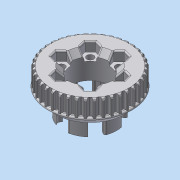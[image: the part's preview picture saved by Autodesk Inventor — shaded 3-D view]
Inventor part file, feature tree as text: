
AUTODESK INVENTOR PART (.ipt)
format: ipt  version: 2017 (Build 210142000, 142)  size: 2,198,016 bytes
history: native  units: in
note: dims shown in document units (in); Inventor stores cm internally (conversion verified against a paired STEP export)
features: extrude x7, other x4, sketch x4, fillet x4, chamfer x3, projected_geometry x2, move_body x1
ambient origin geometry x8: Origin, YZ Plane, XZ Plane, XY Plane, X Axis, Y Axis, Z Axis, Center Point
bodies: Solid1 (feature_tree), Solid3 (feature_tree)
feature tree (25):
  other  "wheelinsertsketch.ipt"
  other  "40t_pulley.ipt"
  extrude  "Extrusion1"  Depth=0.5in TaperAngle=0.0deg
  extrude  "Extrusion2"  Depth=0.3in TaperAngle=0.0deg
  chamfer  "Chamfer1"  Distance=0.25in Angle=45.0deg
  sketch  "Sketch14"  dims[d39=1.1in d40=0.4724in d41=0.0in d42=5.0in d43=0.0in d44=0.05in d45=0.02in d46=0.125in d61=0.1625in d62=0.125in d63=45.0deg d80=0.38in d81=2.3622in d83=360.0deg d85=1.0in d86=0.0in d87=0.2756in d88=0.0in d90=0.4724in d91=0.0in d92=0.0591in d93=0.125in d94=45.0deg d96=0.0394in d102=0.205in d103=0.0787in]
  move_body  "Move Body2"
  extrude  "Extrusion14"  TaperAngle=90.0deg  [1 undecoded]
  chamfer  "Chamfer7"  Distance=0.4724in
  fillet  "Fillet21"  Radius=5.0in
  extrude  "Extrusion6"  Depth=0.05in
  extrude  "hella sketch"  Depth=0.02in
  fillet  "Fillet6"  Radius=0.125in
  fillet  "Fillet7"  Radius=0.1625in
  chamfer  "Chamfer4"  Distance=0.38in
  sketch  "Sketch12"  dims[d3=2.4803in d4=0.3in d5=0.0in d6=0.25in d7=0.125in d8=45.0deg]
  extrude  "Extrusion12"  Depth=2.3622in TaperAngle=360.0deg
  extrude  "Extrusion13"  Depth=1.0in TaperAngle=0.0deg
  fillet  "Fillet18"  Radius=0.2756in
  other  "Solid1::40t_pulley.ipt"
  other  "TaggingFeature2"
  projected_geometry  "Projected Loop2"
  sketch  "Sketch7"  dims[d0=0.3937in d1=0.5in d2=0.0in]
  sketch  "Sketch13"  dims[d34=0.3937in d35=90.0deg d36=0.0in d37=-2.0in d38=0.0in]
  projected_geometry  "Projected Loop4"
note: 1 required parameter value undecoded (feature->parameter linkage not recoverable at this tier; creation-order binding heuristic only, values carry confidence <= 0.55)
